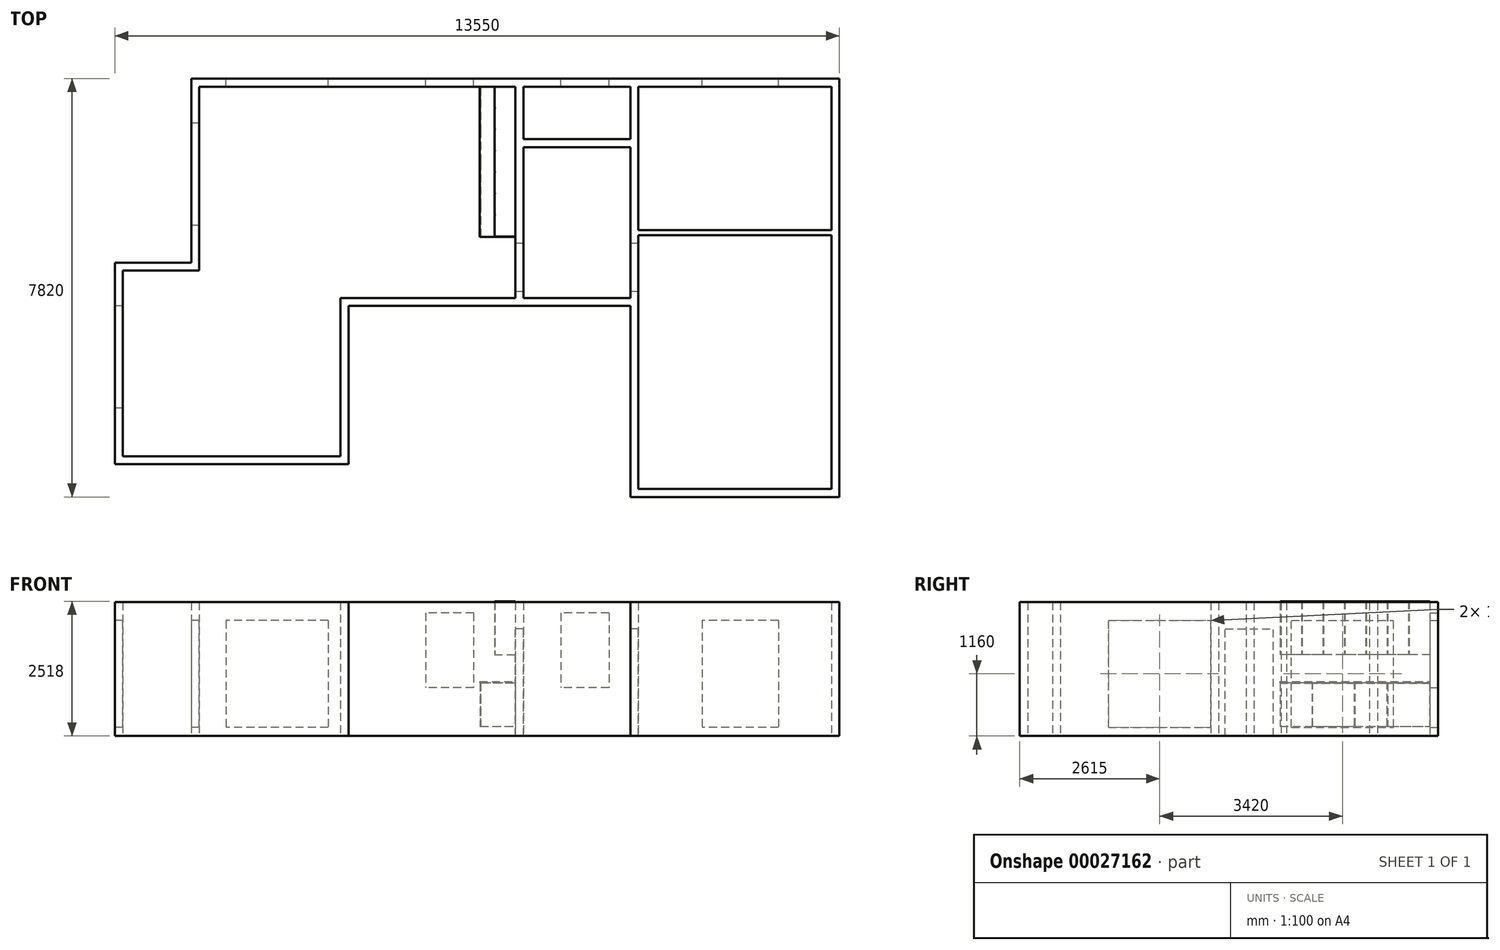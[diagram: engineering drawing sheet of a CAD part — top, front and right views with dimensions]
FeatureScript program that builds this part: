
annotation { "Feature Type Name" : "Feature", "Feature Type Description" : "" }
export const myFeature = defineFeature(function(context is Context, id is Id, definition is map)
    precondition{}
    {
        {
            var Q0;
            Q0=qCreatedBy(makeId("Top.planeOp"),FACE);
            var sketch = newSketch(context, id + "F0", { "sketchPlane" : qUnion([Q0])});
            skLineSegment(sketch, "E0.bottom", {"start": v(-4910, 1000) * mm, "end": v(1000, 1000) * mm});
            skLineSegment(sketch, "E0.top", {"start": v(-2270, -2950) * mm, "end": v(1000, -2950) * mm});
            skLineSegment(sketch, "E0.left", {"start": v(-4910, 1000) * mm, "end": v(-4910, -2440) * mm});
            skLineSegment(sketch, "E0.right", {"start": v(1000, 1000) * mm, "end": v(1000, -2950) * mm});
            skLineSegment(sketch, "E1.bottom", {"start": v(-6340, -2440) * mm, "end": v(-4910, -2440) * mm});
            skLineSegment(sketch, "E1.top", {"start": v(-6340, -5910) * mm, "end": v(-2270, -5910) * mm});
            skLineSegment(sketch, "E1.left", {"start": v(-6340, -2440) * mm, "end": v(-6340, -5910) * mm});
            skLineSegment(sketch, "E1.right", {"start": v(-2270, -2950) * mm, "end": v(-2270, -5910) * mm});
            skLineSegment(sketch, "E2.bottom", {"start": v(1150, 1000) * mm, "end": v(3150, 1000) * mm});
            skLineSegment(sketch, "E2.top", {"start": v(1150, 20) * mm, "end": v(3150, 20) * mm});
            skLineSegment(sketch, "E2.left", {"start": v(1150, 1000) * mm, "end": v(1150, 20) * mm});
            skLineSegment(sketch, "E2.right", {"start": v(3150, 1000) * mm, "end": v(3150, 20) * mm});
            skLineSegment(sketch, "E3.bottom", {"start": v(1150, -130) * mm, "end": v(3150, -130) * mm});
            skLineSegment(sketch, "E3.top", {"start": v(1150, -2950) * mm, "end": v(3150, -2950) * mm});
            skLineSegment(sketch, "E3.left", {"start": v(1150, -130) * mm, "end": v(1150, -2950) * mm});
            skLineSegment(sketch, "E3.right", {"start": v(3150, -130) * mm, "end": v(3150, -2950) * mm});
            skLineSegment(sketch, "E4.bottom", {"start": v(3300, -1780) * mm, "end": v(6910, -1780) * mm});
            skLineSegment(sketch, "E4.top", {"start": v(3300, -6520) * mm, "end": v(6910, -6520) * mm});
            skLineSegment(sketch, "E4.left", {"start": v(3300, -1780) * mm, "end": v(3300, -6520) * mm});
            skLineSegment(sketch, "E4.right", {"start": v(6910, -1780) * mm, "end": v(6910, -6520) * mm});
            skLineSegment(sketch, "E5.bottom", {"start": v(3300, 1000) * mm, "end": v(6910, 1000) * mm});
            skLineSegment(sketch, "E5.top", {"start": v(3300, -1680) * mm, "end": v(6910, -1680) * mm});
            skLineSegment(sketch, "E5.left", {"start": v(3300, 1000) * mm, "end": v(3300, -1680) * mm});
            skLineSegment(sketch, "E5.right", {"start": v(6910, 1000) * mm, "end": v(6910, -1680) * mm});
            skLineSegment(sketch, "E6", {"start": v(-5060, -2290) * mm, "end": v(-6490, -2290) * mm});
            skLineSegment(sketch, "E7", {"start": v(-6490, -2290) * mm, "end": v(-6490, -6060) * mm});
            skLineSegment(sketch, "E8", {"start": v(-6490, -6060) * mm, "end": v(-2120, -6060) * mm});
            skLineSegment(sketch, "E9", {"start": v(-2120, -6060) * mm, "end": v(-2120, -3100) * mm});
            skLineSegment(sketch, "E10", {"start": v(-2120, -3100) * mm, "end": v(3150, -3100) * mm});
            skLineSegment(sketch, "E11", {"start": v(3150, -3100) * mm, "end": v(3150, -6670) * mm});
            skLineSegment(sketch, "E12", {"start": v(3150, -6670) * mm, "end": v(7060, -6670) * mm});
            skLineSegment(sketch, "E13", {"start": v(7060, -6670) * mm, "end": v(7060, 1150) * mm});
            skLineSegment(sketch, "E14", {"start": v(7060, 1150) * mm, "end": v(-5060, 1150) * mm});
            skLineSegment(sketch, "E15", {"start": v(-5060, 1150) * mm, "end": v(-5060, -2290) * mm});
            skSolve(sketch);
        }
        {
            var Q0;
            Q0=makeQuery(id+"F0.imprint","IMPRINT",FACE,{"disambiguationData":[TD([[makeQuery(id+"F0.imprint","IMPRINT",EDGE,{"derivedFrom":sQuery(id+"F0.wireOp",EDGE,"E0.bottom")}),1.0]])]});
            extrude(context, id + "F1", {"entities" : qUnion([Q0]), "depth" : 2500 * mm});
        }
        {
            var Q0;
            Q0=makeQuery(id+"F1.opExtrude","SWEPT_FACE",FACE,{"disambiguationData":[OSD([sQuery(id+"F0.wireOp",EDGE,"E11")])]});
            var sketch = newSketch(context, id + "F2", { "sketchPlane" : qUnion([Q0])});
            skLineSegment(sketch, "E16.bottom", {"start": v(1930, 2000) * mm, "end": v(2830, 2000) * mm});
            skLineSegment(sketch, "E16.top", {"start": v(1930, 0) * mm, "end": v(2830, 0) * mm});
            skLineSegment(sketch, "E16.left", {"start": v(1930, 2000) * mm, "end": v(1930, 0) * mm});
            skLineSegment(sketch, "E16.right", {"start": v(2830, 2000) * mm, "end": v(2830, 0) * mm});
            skSolve(sketch);
        }
        {
            var Q0;
            Q0=makeQuery(id+"F2.imprint","IMPRINT",FACE,{"disambiguationData":[TD([[makeQuery(id+"F2.imprint","IMPRINT",EDGE,{"derivedFrom":sQuery(id+"F2.wireOp",EDGE,"E16.bottom")}),-1.0]])]});
            extrude(context, id + "F3", {"entities" : qUnion([Q0]), "operationType" : NewBodyOperationType.REMOVE, "oppositeDirection" : true, "depth" : 1134.68 * mm, "hasSecondDirection" : true, "secondDirectionOppositeDirection" : false, "secondDirectionDepth" : 3363.62 * mm});
        }
        {
            var Q0;
            Q0=makeQuery(id+"F1.opExtrude","SWEPT_FACE",FACE,{"disambiguationData":[OSD([sQuery(id+"F0.wireOp",EDGE,"E7")])]});
            var sketch = newSketch(context, id + "F4", { "sketchPlane" : qUnion([Q0])});
            skLineSegment(sketch, "E17.bottom", {"start": v(3100, 2160) * mm, "end": v(5010, 2160) * mm});
            skLineSegment(sketch, "E17.top", {"start": v(3100, 160) * mm, "end": v(5010, 160) * mm});
            skLineSegment(sketch, "E17.left", {"start": v(3100, 2160) * mm, "end": v(3100, 160) * mm});
            skLineSegment(sketch, "E17.right", {"start": v(5010, 2160) * mm, "end": v(5010, 160) * mm});
            skSolve(sketch);
        }
        {
            var Q0;
            Q0=makeQuery(id+"F1.opExtrude","SWEPT_FACE",FACE,{"disambiguationData":[OSD([sQuery(id+"F0.wireOp",EDGE,"E15")])]});
            var sketch = newSketch(context, id + "F5", { "sketchPlane" : qUnion([Q0])});
            skLineSegment(sketch, "E18.bottom", {"start": v(-320, 2160) * mm, "end": v(1590, 2160) * mm});
            skLineSegment(sketch, "E18.top", {"start": v(-320, 160) * mm, "end": v(1590, 160) * mm});
            skLineSegment(sketch, "E18.left", {"start": v(-320, 2160) * mm, "end": v(-320, 160) * mm});
            skLineSegment(sketch, "E18.right", {"start": v(1590, 2160) * mm, "end": v(1590, 160) * mm});
            skSolve(sketch);
        }
        {
            var Q0;
            Q0=makeQuery(id+"F5.imprint","IMPRINT",FACE,{"disambiguationData":[TD([[makeQuery(id+"F5.imprint","IMPRINT",EDGE,{"derivedFrom":sQuery(id+"F5.wireOp",EDGE,"E18.bottom")}),-1.0]])]});
            extrude(context, id + "F6", {"entities" : qUnion([Q0]), "operationType" : NewBodyOperationType.REMOVE, "oppositeDirection" : true, "depth" : 414.14 * mm});
        }
        {
            var Q0;
            Q0=makeQuery(id+"F4.imprint","IMPRINT",FACE,{"disambiguationData":[TD([[makeQuery(id+"F4.imprint","IMPRINT",EDGE,{"derivedFrom":sQuery(id+"F4.wireOp",EDGE,"E17.bottom")}),-1.0]])]});
            extrude(context, id + "F7", {"entities" : qUnion([Q0]), "operationType" : NewBodyOperationType.REMOVE, "oppositeDirection" : true, "depth" : 317.38 * mm});
        }
        {
            var Q0;
            Q0=makeQuery(id+"F1.opExtrude","SWEPT_FACE",FACE,{"disambiguationData":[OSD([sQuery(id+"F0.wireOp",EDGE,"E14")])]});
            var sketch = newSketch(context, id + "F8", { "sketchPlane" : qUnion([Q0])});
            skLineSegment(sketch, "E19.bottom", {"start": v(2500, 2160) * mm, "end": v(4410, 2160) * mm});
            skLineSegment(sketch, "E19.top", {"start": v(2500, 160) * mm, "end": v(4410, 160) * mm});
            skLineSegment(sketch, "E19.left", {"start": v(2500, 2160) * mm, "end": v(2500, 160) * mm});
            skLineSegment(sketch, "E19.right", {"start": v(4410, 2160) * mm, "end": v(4410, 160) * mm});
            skSolve(sketch);
        }
        {
            var Q0;
            Q0 = qSketchRegion(id + "F8", true);
            extrude(context, id + "F9", {"entities" : qUnion([Q0]), "operationType" : NewBodyOperationType.REMOVE, "oppositeDirection" : true, "depth" : 1804.37 * mm});
        }
        {
            var Q0;
            Q0=makeQuery(id+"F1.opExtrude","SWEPT_FACE",FACE,{"disambiguationData":[OSD([sQuery(id+"F0.wireOp",EDGE,"E14")])]});
            var sketch = newSketch(context, id + "F10", { "sketchPlane" : qUnion([Q0])});
            skLineSegment(sketch, "E20.bottom", {"start": v(-5920, 2160) * mm, "end": v(-4490, 2160) * mm});
            skLineSegment(sketch, "E20.top", {"start": v(-5920, 160) * mm, "end": v(-4490, 160) * mm});
            skLineSegment(sketch, "E20.left", {"start": v(-5920, 2160) * mm, "end": v(-5920, 160) * mm});
            skLineSegment(sketch, "E20.right", {"start": v(-4490, 2160) * mm, "end": v(-4490, 160) * mm});
            skLineSegment(sketch, "E21.bottom", {"start": v(-220, 2300) * mm, "end": v(680, 2300) * mm});
            skLineSegment(sketch, "E21.top", {"start": v(-220, 900) * mm, "end": v(680, 900) * mm});
            skLineSegment(sketch, "E21.left", {"start": v(-220, 2300) * mm, "end": v(-220, 900) * mm});
            skLineSegment(sketch, "E21.right", {"start": v(680, 2300) * mm, "end": v(680, 900) * mm});
            skLineSegment(sketch, "E22.bottom", {"start": v(-2750, 2300) * mm, "end": v(-1850, 2300) * mm});
            skLineSegment(sketch, "E22.top", {"start": v(-2750, 900) * mm, "end": v(-1850, 900) * mm});
            skLineSegment(sketch, "E22.left", {"start": v(-2750, 2300) * mm, "end": v(-2750, 900) * mm});
            skLineSegment(sketch, "E22.right", {"start": v(-1850, 2300) * mm, "end": v(-1850, 900) * mm});
            skSolve(sketch);
        }
        {
            var Q0;
            Q0=makeQuery(id+"F10.imprint","IMPRINT",FACE,{"disambiguationData":[TD([[makeQuery(id+"F10.imprint","IMPRINT",EDGE,{"derivedFrom":sQuery(id+"F10.wireOp",EDGE,"E20.bottom")}),-1.0]])]});
            extrude(context, id + "F11", {"entities" : qUnion([Q0]), "operationType" : NewBodyOperationType.REMOVE, "oppositeDirection" : true, "depth" : 827.94 * mm});
        }
        {
            var Q0;
            Q0=makeQuery(id+"F10.imprint","IMPRINT",FACE,{"disambiguationData":[TD([[makeQuery(id+"F10.imprint","IMPRINT",EDGE,{"derivedFrom":sQuery(id+"F10.wireOp",EDGE,"E22.bottom")}),-1.0]])]});
            var Q1;
            Q1=makeQuery(id+"F10.imprint","IMPRINT",FACE,{"disambiguationData":[TD([[makeQuery(id+"F10.imprint","IMPRINT",EDGE,{"derivedFrom":sQuery(id+"F10.wireOp",EDGE,"E21.bottom")}),-1.0]])]});
            extrude(context, id + "F12", {"entities" : qUnion([Q0, Q1]), "operationType" : NewBodyOperationType.REMOVE, "oppositeDirection" : true, "depth" : 384.9 * mm});
        }
        {
            var Q0;
            Q0=qCreatedBy(makeId("Top.planeOp"),FACE);
            var sketch = newSketch(context, id + "F13", { "sketchPlane" : qUnion([Q0])});
            skLineSegment(sketch, "E23.bottom", {"start": v(350, -1800) * mm, "end": v(1000, -1800) * mm});
            skLineSegment(sketch, "E23.top", {"start": v(350, 1000) * mm, "end": v(1000, 1000) * mm});
            skLineSegment(sketch, "E23.left", {"start": v(350, -1800) * mm, "end": v(350, 1000) * mm});
            skLineSegment(sketch, "E23.right", {"start": v(1000, -1800) * mm, "end": v(1000, 1000) * mm});
            skSolve(sketch);
        }
        {
            var Q0;
            Q0 = qSketchRegion(id + "F13", true);
            extrude(context, id + "F14", {"entities" : qUnion([Q0]), "depth" : 990 * mm, "hasSecondDirection" : true, "secondDirectionOppositeDirection" : false, "secondDirectionDepth" : 180 * mm});
        }
        {
            var Q0;
            Q0=makeQuery(id+"F14.opExtrude","SWEPT_FACE",FACE,{"disambiguationData":[OSD([sQuery(id+"F13.wireOp",EDGE,"E23.left")])]});
            var sketch = newSketch(context, id + "F15", { "sketchPlane" : qUnion([Q0])});
            skLineSegment(sketch, "E24.bottom", {"start": v(-990, 980) * mm, "end": v(-210, 980) * mm});
            skLineSegment(sketch, "E24.top", {"start": v(-990, 180) * mm, "end": v(-210, 180) * mm});
            skLineSegment(sketch, "E24.left", {"start": v(-990, 980) * mm, "end": v(-990, 180) * mm});
            skLineSegment(sketch, "E24.right", {"start": v(-210, 980) * mm, "end": v(-210, 180) * mm});
            skLineSegment(sketch, "E25.bottom", {"start": v(-200, 180) * mm, "end": v(400, 180) * mm});
            skLineSegment(sketch, "E25.top", {"start": v(-200, 980) * mm, "end": v(400, 980) * mm});
            skLineSegment(sketch, "E25.left", {"start": v(-200, 180) * mm, "end": v(-200, 980) * mm});
            skLineSegment(sketch, "E25.right", {"start": v(400, 180) * mm, "end": v(400, 980) * mm});
            skLineSegment(sketch, "E26.bottom", {"start": v(1200, 180) * mm, "end": v(1800, 180) * mm});
            skLineSegment(sketch, "E26.top", {"start": v(1200, 980) * mm, "end": v(1800, 980) * mm});
            skLineSegment(sketch, "E26.left", {"start": v(1200, 180) * mm, "end": v(1200, 980) * mm});
            skLineSegment(sketch, "E26.right", {"start": v(1800, 180) * mm, "end": v(1800, 980) * mm});
            skLineSegment(sketch, "E27.bottom", {"start": v(410, 180) * mm, "end": v(1190, 180) * mm});
            skLineSegment(sketch, "E27.top", {"start": v(410, 980) * mm, "end": v(1190, 980) * mm});
            skLineSegment(sketch, "E27.left", {"start": v(410, 180) * mm, "end": v(410, 980) * mm});
            skLineSegment(sketch, "E27.right", {"start": v(1190, 180) * mm, "end": v(1190, 980) * mm});
            skSolve(sketch);
        }
        {
            var Q0;
            Q0 = qSketchRegion(id + "F15", true);
            extrude(context, id + "F16", {"entities" : qUnion([Q0]), "operationType" : NewBodyOperationType.ADD, "depth" : 12 * mm});
        }
        {
            var Q0;
            Q0=makeQuery(id+"F14.opExtrude","CAP_FACE",FACE,{"disambiguationData":[OSD([sQuery(id+"F13.wireOp",EDGE,"E23.bottom"),sQuery(id+"F13.wireOp",EDGE,"E23.top"),sQuery(id+"F13.wireOp",EDGE,"E23.left"),sQuery(id+"F13.wireOp",EDGE,"E23.right")])],"isStart":false});
            var sketch = newSketch(context, id + "F17", { "sketchPlane" : qUnion([Q0])});
            skLineSegment(sketch, "E28.bottom", {"start": v(1000, 1000) * mm, "end": v(330, 1000) * mm});
            skLineSegment(sketch, "E28.top", {"start": v(1000, -1810) * mm, "end": v(330, -1810) * mm});
            skLineSegment(sketch, "E28.left", {"start": v(1000, 1000) * mm, "end": v(1000, -1810) * mm});
            skLineSegment(sketch, "E28.right", {"start": v(330, 1000) * mm, "end": v(330, -1810) * mm});
            skSolve(sketch);
        }
        {
            var Q0;
            Q0 = qSketchRegion(id + "F17", true);
            extrude(context, id + "F18", {"entities" : qUnion([Q0]), "operationType" : NewBodyOperationType.ADD, "depth" : 28 * mm});
        }
        {
            var Q0;
            Q0=makeQuery(id+"F1.opExtrude","SWEPT_FACE",FACE,{"disambiguationData":[OSD([sQuery(id+"F0.wireOp",EDGE,"E0.right")])]});
            var sketch = newSketch(context, id + "F19", { "sketchPlane" : qUnion([Q0])});
            skLineSegment(sketch, "E29.bottom", {"start": v(-1000, 2518) * mm, "end": v(1800, 2518) * mm});
            skLineSegment(sketch, "E29.top", {"start": v(-1000, 1518) * mm, "end": v(1800, 1518) * mm});
            skLineSegment(sketch, "E29.left", {"start": v(-1000, 2518) * mm, "end": v(-1000, 1518) * mm});
            skLineSegment(sketch, "E29.right", {"start": v(1800, 2518) * mm, "end": v(1800, 1518) * mm});
            skSolve(sketch);
        }
        {
            var Q0;
            Q0 = qSketchRegion(id + "F19", true);
            extrude(context, id + "F20", {"entities" : qUnion([Q0]), "depth" : 380 * mm});
        }
        {
            var Q0;
            Q0=makeQuery(id+"F20.opExtrude","CAP_FACE",FACE,{"disambiguationData":[OSD([sQuery(id+"F19.wireOp",EDGE,"E29.bottom"),sQuery(id+"F19.wireOp",EDGE,"E29.top"),sQuery(id+"F19.wireOp",EDGE,"E29.left"),sQuery(id+"F19.wireOp",EDGE,"E29.right")])],"isStart":false});
            var sketch = newSketch(context, id + "F21", { "sketchPlane" : qUnion([Q0])});
            skLineSegment(sketch, "E30.bottom", {"start": v(-1000, 2518) * mm, "end": v(-610, 2518) * mm});
            skLineSegment(sketch, "E30.top", {"start": v(-1000, 1518) * mm, "end": v(-610, 1518) * mm});
            skLineSegment(sketch, "E30.left", {"start": v(-1000, 2518) * mm, "end": v(-1000, 1518) * mm});
            skLineSegment(sketch, "E30.right", {"start": v(-610, 2518) * mm, "end": v(-610, 1518) * mm});
            skLineSegment(sketch, "E31.bottom", {"start": v(-600, 2518) * mm, "end": v(-210, 2518) * mm});
            skLineSegment(sketch, "E31.top", {"start": v(-600, 1518) * mm, "end": v(-210, 1518) * mm});
            skLineSegment(sketch, "E31.left", {"start": v(-600, 2518) * mm, "end": v(-600, 1518) * mm});
            skLineSegment(sketch, "E31.right", {"start": v(-210, 2518) * mm, "end": v(-210, 1518) * mm});
            skLineSegment(sketch, "E32.bottom", {"start": v(-200, 2518) * mm, "end": v(190, 2518) * mm});
            skLineSegment(sketch, "E32.top", {"start": v(-200, 1518) * mm, "end": v(190, 1518) * mm});
            skLineSegment(sketch, "E32.left", {"start": v(-200, 2518) * mm, "end": v(-200, 1518) * mm});
            skLineSegment(sketch, "E32.right", {"start": v(190, 2518) * mm, "end": v(190, 1518) * mm});
            skLineSegment(sketch, "E33.bottom", {"start": v(200, 2518) * mm, "end": v(590, 2518) * mm});
            skLineSegment(sketch, "E33.top", {"start": v(200, 1518) * mm, "end": v(590, 1518) * mm});
            skLineSegment(sketch, "E33.left", {"start": v(200, 2518) * mm, "end": v(200, 1518) * mm});
            skLineSegment(sketch, "E33.right", {"start": v(590, 2518) * mm, "end": v(590, 1518) * mm});
            skLineSegment(sketch, "E34.bottom", {"start": v(600, 2518) * mm, "end": v(990, 2518) * mm});
            skLineSegment(sketch, "E34.top", {"start": v(600, 1518) * mm, "end": v(990, 1518) * mm});
            skLineSegment(sketch, "E34.left", {"start": v(600, 2518) * mm, "end": v(600, 1518) * mm});
            skLineSegment(sketch, "E34.right", {"start": v(990, 2518) * mm, "end": v(990, 1518) * mm});
            skLineSegment(sketch, "E35.bottom", {"start": v(1000, 2518) * mm, "end": v(1390, 2518) * mm});
            skLineSegment(sketch, "E35.top", {"start": v(1000, 1518) * mm, "end": v(1390, 1518) * mm});
            skLineSegment(sketch, "E35.left", {"start": v(1000, 2518) * mm, "end": v(1000, 1518) * mm});
            skLineSegment(sketch, "E35.right", {"start": v(1390, 2518) * mm, "end": v(1390, 1518) * mm});
            skLineSegment(sketch, "E36.bottom", {"start": v(1400, 2518) * mm, "end": v(1800, 2518) * mm});
            skLineSegment(sketch, "E36.top", {"start": v(1400, 1518) * mm, "end": v(1800, 1518) * mm});
            skLineSegment(sketch, "E36.left", {"start": v(1400, 2518) * mm, "end": v(1400, 1518) * mm});
            skLineSegment(sketch, "E36.right", {"start": v(1800, 2518) * mm, "end": v(1800, 1518) * mm});
            skSolve(sketch);
        }
        {
            var Q0;
            Q0=makeQuery(id+"F21.imprint","IMPRINT",FACE,{"disambiguationData":[TD([[makeQuery(id+"F21.imprint","IMPRINT",EDGE,{"derivedFrom":sQuery(id+"F21.wireOp",EDGE,"E30.bottom")}),-1.0]])]});
            var Q1;
            Q1=makeQuery(id+"F21.imprint","IMPRINT",FACE,{"disambiguationData":[TD([[makeQuery(id+"F21.imprint","IMPRINT",EDGE,{"derivedFrom":sQuery(id+"F21.wireOp",EDGE,"E31.bottom")}),-1.0]])]});
            var Q2;
            Q2=makeQuery(id+"F21.imprint","IMPRINT",FACE,{"disambiguationData":[TD([[makeQuery(id+"F21.imprint","IMPRINT",EDGE,{"derivedFrom":sQuery(id+"F21.wireOp",EDGE,"E32.bottom")}),-1.0]])]});
            var Q3;
            Q3=makeQuery(id+"F21.imprint","IMPRINT",FACE,{"disambiguationData":[TD([[makeQuery(id+"F21.imprint","IMPRINT",EDGE,{"derivedFrom":sQuery(id+"F21.wireOp",EDGE,"E33.bottom")}),-1.0]])]});
            var Q4;
            Q4=makeQuery(id+"F21.imprint","IMPRINT",FACE,{"disambiguationData":[TD([[makeQuery(id+"F21.imprint","IMPRINT",EDGE,{"derivedFrom":sQuery(id+"F21.wireOp",EDGE,"E34.bottom")}),-1.0]])]});
            var Q5;
            Q5=makeQuery(id+"F21.imprint","IMPRINT",FACE,{"disambiguationData":[TD([[makeQuery(id+"F21.imprint","IMPRINT",EDGE,{"derivedFrom":sQuery(id+"F21.wireOp",EDGE,"E35.bottom")}),-1.0]])]});
            var Q6;
            Q6=makeQuery(id+"F21.imprint","IMPRINT",FACE,{"disambiguationData":[TD([[makeQuery(id+"F21.imprint","IMPRINT",EDGE,{"derivedFrom":sQuery(id+"F21.wireOp",EDGE,"E36.bottom")}),-1.0]])]});
            extrude(context, id + "F22", {"entities" : qUnion([Q0, Q1, Q2, Q3, Q4, Q5, Q6]), "operationType" : NewBodyOperationType.ADD, "depth" : 10 * mm});
        }
    });
